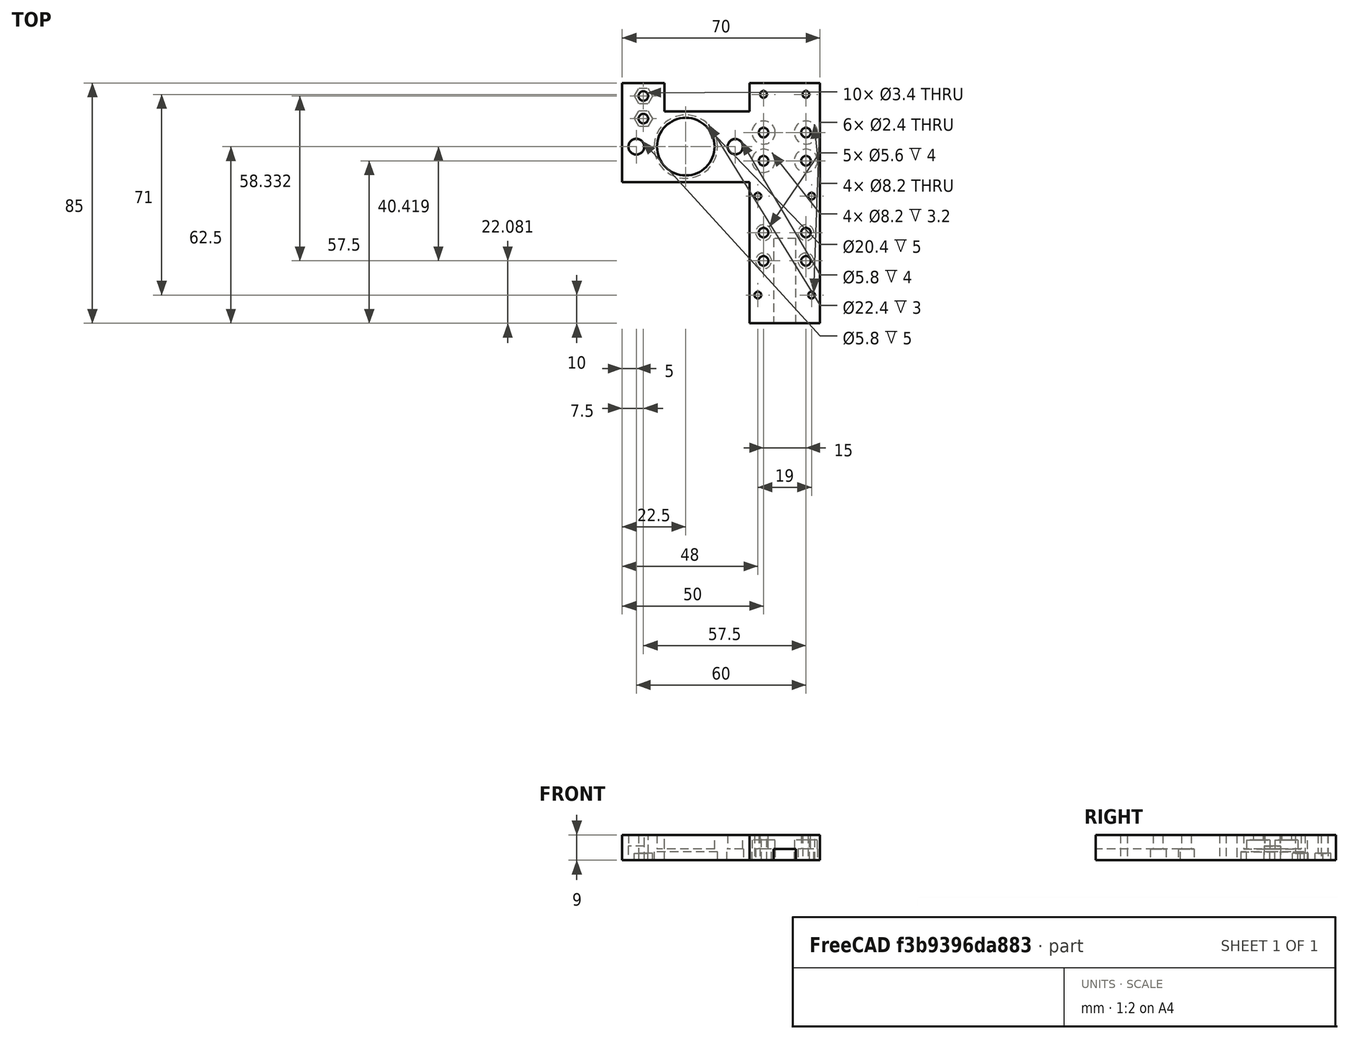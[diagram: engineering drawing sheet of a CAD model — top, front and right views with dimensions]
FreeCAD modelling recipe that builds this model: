
FCSTD DOCUMENT  (FreeCAD 0.18.4R)
Label: down_left_magnet_arm
License: All rights reserved
LicenseURL: http://en.wikipedia.org/wiki/All_rights_reserved
objects: Sketcher::SketchObject×15, PartDesign::Pocket×9, PartDesign::Pad×6, Mesh::Feature×1, PartDesign::Body×1
note: 46 computed .brp shape members not serialized (recipe doc carries the construction recipe); baked Part::Feature solids carry a one-line shape summary decoded from their .brp

FEATURE [Sketcher::SketchObject] Sketch
  MapMode = 5
  Support = -> [XY_Plane]
  sketch-geometry (10):
    g0: LineSegment StartX=-30 StartY=12.5 StartZ=0 EndX=30 EndY=12.5 EndZ=0
    g1: LineSegment StartX=30 StartY=12.5 StartZ=0 EndX=30 EndY=-12.5 EndZ=0
    g2: LineSegment StartX=30 StartY=-12.5 StartZ=0 EndX=-30 EndY=-12.5 EndZ=0
    g3: LineSegment StartX=-30 StartY=-12.5 StartZ=0 EndX=-30 EndY=12.5 EndZ=0
    g4: Circle CenterX=10 CenterY=5 CenterZ=0 NormalX=0 NormalY=0 NormalZ=1 AngleXU=0 Radius=1.7
    g5: Circle CenterX=25 CenterY=5 CenterZ=0 NormalX=0 NormalY=0 NormalZ=1 AngleXU=0 Radius=1.7
    g6: Circle CenterX=10 CenterY=-5 CenterZ=0 NormalX=0 NormalY=0 NormalZ=1 AngleXU=0 Radius=1.7
    g7: Circle CenterX=25 CenterY=-5 CenterZ=0 NormalX=0 NormalY=0 NormalZ=1 AngleXU=0 Radius=1.7
    g8: Circle CenterX=-17.5 CenterY=0 CenterZ=0 NormalX=0 NormalY=0 NormalZ=1 AngleXU=0 Radius=10.2
    g9: Circle CenterX=-9e-16 CenterY=0 CenterZ=0 NormalX=0 NormalY=0 NormalZ=1 AngleXU=0 Radius=2.7
  constraints (26):
    c: Coincident(g0,g1)
    c: Coincident(g1,g2)
    c: Coincident(g2,g3)
    c: Coincident(g3,g0)
    c: Horizontal(g2)
    c: Vertical(g1)
    c: Symmetric(g0,g0,g-2)
    c: Symmetric(g0,g2,g-1)
    c: DistanceX(g0,g0) = 60
    c: DistanceY(g3,g3) = 25
    c: Symmetric(g7,g5,g-1)
    c: Symmetric(g4,g6,g-1)
    c: Distance(g6,g7) = 15
    c: Distance(g4,g6) = 10
    c: Horizontal(g5,g4)
    c: Radius(g4) = 1.7
    c: Radius(g5) = 1.7
    c: Radius(g7) = 1.7
    c: Radius(g6) = 1.7
    c: Distance(g5,g1) = 5
    c: Radius(g8) = 10.2
    c: PointOnObject(g8,g-1)
    c: Distance(g8,g3) = 12.5
    c: PointOnObject(g9,g-1)
    c: Distance(g9,g8) = 17.5
    c: Radius(g9) = 2.7
FEATURE [PartDesign::Pad] Pad
  Length = 5
  Length2 = 100
  Profile = -> Sketch
  Type = 0
FEATURE [Sketcher::SketchObject] Sketch001
  ExternalGeometry = -> [Pad]
  MapMode = 5
  Placement = pos=(0,0,0) rot=(1,0,0;3.14159rad)
  Support = -> [Pad]
  sketch-geometry (4):
    g0: Circle CenterX=25 CenterY=5 CenterZ=0 NormalX=0 NormalY=0 NormalZ=1 AngleXU=0 Radius=4.1
    g1: Circle CenterX=25 CenterY=-5 CenterZ=0 NormalX=0 NormalY=0 NormalZ=1 AngleXU=0 Radius=4.1
    g2: Circle CenterX=10 CenterY=5 CenterZ=0 NormalX=0 NormalY=0 NormalZ=1 AngleXU=0 Radius=4.1
    g3: Circle CenterX=10 CenterY=-5 CenterZ=0 NormalX=0 NormalY=0 NormalZ=1 AngleXU=0 Radius=4.1
  constraints (8):
    c: Coincident(g0,g-4)
    c: Coincident(g1,g-5)
    c: Coincident(g2,g-6)
    c: Radius(g0) = 4.1
    c: Radius(g1) = 4.1
    c: Radius(g2) = 4.1
    c: Coincident(g3,g-11)
    c: Radius(g3) = 4.1
FEATURE [PartDesign::Pocket] Pocket001
  BaseFeature = -> Pad
  Length = 3.2
  Length2 = 100
  Profile = -> Sketch001
  Type = 0
FEATURE [Sketcher::SketchObject] Sketch002
  ExternalGeometry = -> [Pocket001]
  MapMode = 5
  Placement = pos=(0,0,0) rot=(1,0,0;3.14159rad)
  Support = -> [Pocket001]
  sketch-geometry (9):
    g0: LineSegment StartX=-30 StartY=12.5 StartZ=0 EndX=30 EndY=12.5 EndZ=0
    g1: LineSegment StartX=30 StartY=12.5 StartZ=0 EndX=30 EndY=-12.5 EndZ=0
    g2: LineSegment StartX=30 StartY=-12.5 StartZ=0 EndX=-30 EndY=-12.5 EndZ=0
    g3: LineSegment StartX=-30 StartY=-12.5 StartZ=0 EndX=-30 EndY=12.5 EndZ=0
    g4: Circle CenterX=0 CenterY=0 CenterZ=0 NormalX=0 NormalY=0 NormalZ=1 AngleXU=0 Radius=2.9
    g5: Circle CenterX=10 CenterY=5 CenterZ=0 NormalX=0 NormalY=0 NormalZ=1 AngleXU=0 Radius=4.1
    g6: Circle CenterX=10 CenterY=-5 CenterZ=0 NormalX=0 NormalY=0 NormalZ=1 AngleXU=0 Radius=4.1
    g7: Circle CenterX=25 CenterY=5 CenterZ=0 NormalX=0 NormalY=0 NormalZ=1 AngleXU=0 Radius=4.1
    g8: Circle CenterX=25 CenterY=-5 CenterZ=0 NormalX=0 NormalY=0 NormalZ=1 AngleXU=0 Radius=4.1
  constraints (20):
    c: Coincident(g0,g1)
    c: Coincident(g1,g2)
    c: Coincident(g2,g3)
    c: Coincident(g3,g0)
    c: Horizontal(g0)
    c: Horizontal(g2)
    c: Vertical(g1)
    c: Vertical(g3)
    c: Coincident(g0,g-6)
    c: Coincident(g1,g-5)
    c: Coincident(g4,g-1)
    c: Coincident(g5,g-8)
    c: Coincident(g6,g-9)
    c: Coincident(g7,g-10)
    c: Coincident(g8,g-11)
    c: Radius(g4) = 2.9
    c: Radius(g5) = 4.1
    c: Radius(g7) = 4.1
    c: Radius(g8) = 4.1
    c: Radius(g6) = 4.1
FEATURE [PartDesign::Pad] Pad001
  BaseFeature = -> Pocket001
  Length = 4
  Length2 = 100
  Profile = -> Sketch002
  Type = 0
FEATURE [Sketcher::SketchObject] Sketch003
  ExternalGeometry = -> [Pad001]
  MapMode = 5
  Placement = pos=(0,0,-4) rot=(1,0,0;3.14159rad)
  Support = -> [Pad001]
  sketch-geometry (1):
    g0: Circle CenterX=-17.5 CenterY=0 CenterZ=0 NormalX=0 NormalY=0 NormalZ=1 AngleXU=0 Radius=11.2
  constraints (3):
    c: PointOnObject(g0,g-1)
    c: Radius(g0) = 11.2
    c: Distance(g0,g-4) = 12.5
FEATURE [PartDesign::Pocket] Pocket
  BaseFeature = -> Pad001
  Length = 3
  Length2 = 100
  Profile = -> Sketch003
  Type = 0
FEATURE [Sketcher::SketchObject] Sketch004
  ExternalGeometry = -> [Pocket]
  MapMode = 5
  Placement = pos=(-30,0,0) rot=(0.57735,-0.57735,-0.57735;2.0944rad)
  Support = -> [Pocket]
  sketch-geometry (4):
    g0: LineSegment StartX=12.5 StartY=-4 StartZ=0 EndX=-12.5 EndY=-4 EndZ=0
    g1: LineSegment StartX=-12.5 StartY=-4 StartZ=0 EndX=-12.5 EndY=5 EndZ=0
    g2: LineSegment StartX=-12.5 StartY=5 StartZ=0 EndX=12.5 EndY=5 EndZ=0
    g3: LineSegment StartX=12.5 StartY=5 StartZ=0 EndX=12.5 EndY=-4 EndZ=0
  constraints (12):
    c: Coincident(g0,g1)
    c: Coincident(g1,g2)
    c: Coincident(g2,g3)
    c: Coincident(g3,g0)
    c: Horizontal(g2)
    c: Vertical(g1)
    c: Vertical(g3)
    c: PointOnObject(g0,g-3)
    c: DistanceX(g0,g0) = 25
    c: Symmetric(g0,g0,g-2)
    c: PointOnObject(g1,g-4)
    c: Distance(g-3) = 25
FEATURE [PartDesign::Pad] Pad002
  BaseFeature = -> Pocket
  Length = 10
  Length2 = 100
  Profile = -> Sketch004
  Type = 0
FEATURE [Sketcher::SketchObject] Sketch005
  ExternalGeometry = -> [Pad002]
  MapMode = 5
  Placement = pos=(0,0,-4) rot=(1,0,0;3.14159rad)
  Support = -> [Pad002]
  sketch-geometry (1):
    g0: Circle CenterX=-35 CenterY=0 CenterZ=0 NormalX=0 NormalY=0 NormalZ=1 AngleXU=0 Radius=2.9
  constraints (3):
    c: PointOnObject(g0,g-1)
    c: Distance(g-3,g0) = 17.5
    c: Radius(g0) = 2.9
FEATURE [PartDesign::Pocket] Pocket002
  BaseFeature = -> Pad002
  Length = 5
  Length2 = 100
  Profile = -> Sketch005
  Type = 0
FEATURE [Mesh::Feature] belt_support_left001
  Placement = pos=(-15,-17,5) rot=(0,0,1;0rad)
FEATURE [Sketcher::SketchObject] Sketch006
  ExternalGeometry = -> [Pocket002]
  MapMode = 5
  Placement = pos=(0,-12.5,0) rot=(1,0,0;1.5708rad)
  Support = -> [Pocket002]
  sketch-geometry (4):
    g0: LineSegment StartX=30 StartY=5 StartZ=0 EndX=5 EndY=5 EndZ=0
    g1: LineSegment StartX=5 StartY=5 StartZ=0 EndX=5 EndY=-4 EndZ=0
    g2: LineSegment StartX=5 StartY=-4 StartZ=0 EndX=30 EndY=-4 EndZ=0
    g3: LineSegment StartX=30 StartY=-4 StartZ=0 EndX=30 EndY=5 EndZ=0
  constraints (11):
    c: Coincident(g0,g1)
    c: Coincident(g1,g2)
    c: Coincident(g2,g3)
    c: Coincident(g3,g0)
    c: Horizontal(g0)
    c: Horizontal(g2)
    c: Vertical(g1)
    c: Vertical(g3)
    c: Coincident(g0,g-4)
    c: PointOnObject(g1,g-5)
    c: DistanceX(g0,g0) = 25
FEATURE [PartDesign::Pad] Pad003
  BaseFeature = -> Pocket002
  Length = 50
  Length2 = 100
  Profile = -> Sketch006
  Type = 0
FEATURE [Sketcher::SketchObject] Sketch007
  ExternalGeometry = -> [Pad003]
  MapMode = 5
  Placement = pos=(0,12.5,0) rot=(0,0.707107,0.707107;3.14159rad)
  Support = -> [Pad003]
  sketch-geometry (4):
    g0: LineSegment StartX=-30 StartY=5 StartZ=0 EndX=-5 EndY=5 EndZ=0
    g1: LineSegment StartX=-5 StartY=5 StartZ=0 EndX=-5 EndY=-4 EndZ=0
    g2: LineSegment StartX=-5 StartY=-4 StartZ=0 EndX=-30 EndY=-4 EndZ=0
    g3: LineSegment StartX=-30 StartY=-4 StartZ=0 EndX=-30 EndY=5 EndZ=0
  constraints (11):
    c: Coincident(g0,g1)
    c: Coincident(g1,g2)
    c: Coincident(g2,g3)
    c: Coincident(g3,g0)
    c: Horizontal(g0)
    c: Horizontal(g2)
    c: Vertical(g1)
    c: Vertical(g3)
    c: PointOnObject(g1,g-3)
    c: DistanceX(g0,g0) = 25
    c: Coincident(g-4,g0)
FEATURE [PartDesign::Pad] Pad004
  BaseFeature = -> Pad003
  Length = 10
  Length2 = 100
  Profile = -> Sketch007
  Type = 0
FEATURE [Sketcher::SketchObject] Sketch008
  ExternalGeometry = -> [Pad004]
  MapMode = 5
  Placement = pos=(0,-9e-16,-4) rot=(1,0,0;3.14159rad)
  Support = -> [Pad004]
  sketch-geometry (6):
    g0: Circle CenterX=10 CenterY=40.4193 CenterZ=0 NormalX=0 NormalY=0 NormalZ=1 AngleXU=0 Radius=1.7
    g1: Circle CenterX=25 CenterY=40.4193 CenterZ=0 NormalX=0 NormalY=0 NormalZ=1 AngleXU=0 Radius=1.7
    g2: Circle CenterX=10 CenterY=30.4193 CenterZ=0 NormalX=0 NormalY=0 NormalZ=1 AngleXU=0 Radius=1.7
    g3: Circle CenterX=25 CenterY=30.4193 CenterZ=0 NormalX=0 NormalY=0 NormalZ=1 AngleXU=0 Radius=1.7
    g4: Circle CenterX=10 CenterY=-18.5 CenterZ=0 NormalX=0 NormalY=0 NormalZ=1 AngleXU=0 Radius=1.2
    g5: Circle CenterX=25 CenterY=-18.5 CenterZ=0 NormalX=0 NormalY=0 NormalZ=1 AngleXU=0 Radius=1.2
  constraints (17):
    c: Horizontal(g0,g1)
    c: Horizontal(g2,g3)
    c: Horizontal(g4,g5)
    c: Vertical(g0,g2)
    c: Vertical(g2,g4)
    c: Vertical(g1,g3)
    c: Vertical(g3,g5)
    c: Radius(g0) = 1.7
    c: Radius(g1) = 1.7
    c: Radius(g2) = 1.7
    c: Radius(g3) = 1.7
    c: Radius(g4) = 1.2
    c: Radius(g5) = 1.2
    c: Distance(g0,g1) = 15
    c: Vertical(g2,g-3)
    c: Distance(g2,g0) = 10
    c: Distance(g4,g-4) = 6
FEATURE [PartDesign::Pocket] Pocket003
  BaseFeature = -> Pad004
  Length = 9
  Length2 = 100
  Profile = -> Sketch008
  Type = 0
FEATURE [Sketcher::SketchObject] Sketch009
  ExternalGeometry = -> [Pocket003]
  MapMode = 5
  Placement = pos=(0,-9e-16,-4) rot=(1,0,0;3.14159rad)
  Support = -> [Pocket003]
  sketch-geometry (8):
    g0: LineSegment StartX=13.5 StartY=72.5 StartZ=0 EndX=21.5 EndY=72.5 EndZ=0
    g1: LineSegment StartX=21.5 StartY=72.5 StartZ=0 EndX=21.5 EndY=32.5 EndZ=0
    g2: LineSegment StartX=21.5 StartY=32.5 StartZ=0 EndX=13.5 EndY=32.5 EndZ=0
    g3: LineSegment StartX=13.5 StartY=32.5 StartZ=0 EndX=13.5 EndY=72.5 EndZ=0
    g4: Circle CenterX=10 CenterY=40.4193 CenterZ=0 NormalX=0 NormalY=0 NormalZ=1 AngleXU=0 Radius=2.8
    g5: Circle CenterX=10 CenterY=30.4193 CenterZ=0 NormalX=0 NormalY=0 NormalZ=1 AngleXU=0 Radius=2.8
    g6: Circle CenterX=25 CenterY=40.4193 CenterZ=0 NormalX=0 NormalY=0 NormalZ=1 AngleXU=0 Radius=2.8
    g7: Circle CenterX=25 CenterY=30.4193 CenterZ=0 NormalX=0 NormalY=0 NormalZ=1 AngleXU=0 Radius=2.8
  constraints (20):
    c: Coincident(g0,g1)
    c: Coincident(g1,g2)
    c: Coincident(g2,g3)
    c: Coincident(g3,g0)
    c: Horizontal(g0)
    c: Horizontal(g2)
    c: Vertical(g1)
    c: Vertical(g3)
    c: DistanceX(g2,g2) = 8
    c: DistanceY(g3,g3) = 40
    c: Distance(g1,g-3) = 20
    c: Distance(g-4,g3) = 3.5
    c: Coincident(g4,g-7)
    c: Coincident(g5,g-4)
    c: Coincident(g6,g-6)
    c: Coincident(g7,g-5)
    c: Radius(g6) = 2.8
    c: Radius(g4) = 2.8
    c: Radius(g5) = 2.8
    c: Radius(g7) = 2.8
FEATURE [PartDesign::Pocket] Pocket004
  BaseFeature = -> Pocket003
  Length = 4
  Length2 = 100
  Profile = -> Sketch009
  Type = 0
FEATURE [Sketcher::SketchObject] Sketch010
  ExternalGeometry = -> [Pocket004]
  MapMode = 5
  Placement = pos=(0,-9e-16,-4) rot=(1,0,0;3.14159rad)
  Support = -> [Pocket004]
  sketch-geometry (4):
    g0: Circle CenterX=27 CenterY=52.5 CenterZ=0 NormalX=0 NormalY=0 NormalZ=1 AngleXU=0 Radius=1.2
    g1: Circle CenterX=8 CenterY=17.5 CenterZ=0 NormalX=0 NormalY=0 NormalZ=1 AngleXU=0 Radius=1.2
    g2: Circle CenterX=27 CenterY=17.5 CenterZ=0 NormalX=0 NormalY=0 NormalZ=1 AngleXU=0 Radius=1.2
    g3: Circle CenterX=8 CenterY=52.5 CenterZ=0 NormalX=0 NormalY=0 NormalZ=1 AngleXU=0 Radius=1.2
  constraints (12):
    c: Radius(g0) = 1.2
    c: Radius(g1) = 1.2
    c: Radius(g2) = 1.2
    c: Horizontal(g1,g2)
    c: Vertical(g0,g2)
    c: Distance(g1,g2) = 19
    c: Horizontal(g3,g0)
    c: Radius(g3) = 1.2
    c: Distance(g3,g0) = 19
    c: Distance(g3,g-6) = 3
    c: Distance(g3,g-4) = 10
    c: Distance(g1,g-3) = 5
FEATURE [PartDesign::Pocket] Pocket005
  BaseFeature = -> Pocket004
  Length = 9
  Length2 = 100
  Profile = -> Sketch010
  Type = 0
FEATURE [Sketcher::SketchObject] Sketch011
  ExternalGeometry = -> [Pocket005]
  MapMode = 5
  Placement = pos=(0,0,1) rot=(1,0,0;3.14159rad)
  Support = -> [Pocket005]
  sketch-geometry (1):
    g0: Circle CenterX=-35 CenterY=0 CenterZ=0 NormalX=0 NormalY=0 NormalZ=1 AngleXU=0 Radius=2.8
  constraints (2):
    c: Coincident(g0,g-3)
    c: Radius(g0) = 2.8
FEATURE [PartDesign::Pocket] Pocket006
  BaseFeature = -> Pocket005
  Length = 4
  Length2 = 100
  Profile = -> Sketch011
  Type = 0
FEATURE [Sketcher::SketchObject] Sketch013
  ExternalGeometry = -> [Pocket006]
  MapMode = 5
  Placement = pos=(0,12.5,0) rot=(0,0.707107,0.707107;3.14159rad)
  Support = -> [Pocket006]
  sketch-geometry (4):
    g0: LineSegment StartX=40 StartY=-4 StartZ=0 EndX=25 EndY=-4 EndZ=0
    g1: LineSegment StartX=25 StartY=-4 StartZ=0 EndX=25 EndY=5 EndZ=0
    g2: LineSegment StartX=25 StartY=5 StartZ=0 EndX=40 EndY=5 EndZ=0
    g3: LineSegment StartX=40 StartY=5 StartZ=0 EndX=40 EndY=-4 EndZ=0
  constraints (11):
    c: Coincident(g0,g1)
    c: Coincident(g1,g2)
    c: Coincident(g2,g3)
    c: Coincident(g3,g0)
    c: Horizontal(g0)
    c: Horizontal(g2)
    c: Vertical(g1)
    c: Vertical(g3)
    c: Coincident(g0,g-4)
    c: PointOnObject(g1,g-5)
    c: DistanceX(g2,g2) = 15
FEATURE [PartDesign::Pad] Pad005
  BaseFeature = -> Pocket006
  Length = 10
  Length2 = 100
  Profile = -> Sketch013
  Type = 0
FEATURE [Sketcher::SketchObject] Sketch014
  ExternalGeometry = -> [Pad005]
  MapMode = 5
  Placement = pos=(0,-9e-16,-4) rot=(1,0,0;3.14159rad)
  Support = -> [Pad005]
  sketch-geometry (14):
    g0: LineSegment StartX=-30.9 StartY=-12.6838 StartZ=0 EndX=-29.3 EndY=-9.91247 EndZ=0
    g1: LineSegment StartX=-29.3 StartY=-9.91247 StartZ=0 EndX=-30.9 EndY=-7.14119 EndZ=0
    g2: LineSegment StartX=-30.9 StartY=-7.14119 StartZ=0 EndX=-34.1 EndY=-7.14119 EndZ=0
    g3: LineSegment StartX=-34.1 StartY=-7.14119 StartZ=0 EndX=-35.7 EndY=-9.91247 EndZ=0
    g4: LineSegment StartX=-35.7 StartY=-9.91247 StartZ=0 EndX=-34.1 EndY=-12.6838 EndZ=0
    g5: LineSegment StartX=-34.1 StartY=-12.6838 StartZ=0 EndX=-30.9 EndY=-12.6838 EndZ=0
    g6: Circle [constr] CenterX=-32.5 CenterY=-9.91247 CenterZ=0 NormalX=0 NormalY=0 NormalZ=1 AngleXU=0 Radius=3.2
    g7: LineSegment StartX=-30.9 StartY=-20.6838 StartZ=0 EndX=-29.3 EndY=-17.9125 EndZ=0
    g8: LineSegment StartX=-29.3 StartY=-17.9125 StartZ=0 EndX=-30.9 EndY=-15.1412 EndZ=0
    g9: LineSegment StartX=-30.9 StartY=-15.1412 StartZ=0 EndX=-34.1 EndY=-15.1412 EndZ=0
    g10: LineSegment StartX=-34.1 StartY=-15.1412 StartZ=0 EndX=-35.7 EndY=-17.9125 EndZ=0
    g11: LineSegment StartX=-35.7 StartY=-17.9125 StartZ=0 EndX=-34.1 EndY=-20.6838 EndZ=0
    g12: LineSegment StartX=-34.1 StartY=-20.6838 StartZ=0 EndX=-30.9 EndY=-20.6838 EndZ=0
    g13: Circle [constr] CenterX=-32.5 CenterY=-17.9125 CenterZ=0 NormalX=0 NormalY=0 NormalZ=1 AngleXU=0 Radius=3.2
  constraints (33):
    c: Coincident(g0,g1)
    c: Coincident(g1,g2)
    c: Coincident(g2,g3)
    c: Coincident(g3,g4)
    c: Coincident(g4,g5)
    c: Coincident(g5,g0)
    c: Equal(g0, g1-g5) x5
    c: PointOnObject(g0,g6)
    c: PointOnObject(g1,g6)
    c: PointOnObject(g2,g6)
    c: PointOnObject(g3,g6)
    c: PointOnObject(g4,g6)
    c: PointOnObject(g5,g6)
    c: Coincident(g7,g8)
    c: Coincident(g8,g9)
    c: Coincident(g9,g10)
    c: Coincident(g10,g11)
    c: Coincident(g11,g12)
    c: Coincident(g12,g7)
    c: Equal(g7, g8-g12) x5
    c: PointOnObject(g7,g13)
    c: PointOnObject(g8,g13)
    c: PointOnObject(g9,g13)
    c: PointOnObject(g10,g13)
    c: PointOnObject(g11,g13)
    c: PointOnObject(g12,g13)
    c: Vertical(g13,g6)
    c: Radius(g6) = 3.2
    c: Radius(g13) = 3.2
    c: Distance(g13,g6) = 8
    c: Vertical(g0,g8)
    c: Distance(g13,g-4) = 7.5
    c: Parallel(g9,g5)
FEATURE [PartDesign::Pocket] Pocket007
  BaseFeature = -> Pad005
  Length = 2.5
  Length2 = 100
  Profile = -> Sketch014
  Type = 0
FEATURE [Sketcher::SketchObject] Sketch015
  ExternalGeometry = -> [Pocket007]
  MapMode = 5
  Placement = pos=(0,-2e-16,-1.5) rot=(1,0,0;3.14159rad)
  Support = -> [Pocket007]
  sketch-geometry (2):
    g0: Circle CenterX=-32.5 CenterY=-9.91247 CenterZ=0 NormalX=0 NormalY=0 NormalZ=1 AngleXU=0 Radius=1.7
    g1: Circle CenterX=-32.5 CenterY=-17.9125 CenterZ=0 NormalX=0 NormalY=0 NormalZ=1 AngleXU=0 Radius=1.7
  constraints (7):
    c: Radius(g1) = 1.7
    c: Radius(g0) = 1.7
    c: Distance(g-4,g-3) = 6.4
    c: Distance(g0,g-3) = 3.2
    c: Distance(g0,g-3) = 3.2
    c: Distance(g1,g-5) = 3.2
    c: Distance(g1,g-6) = 3.2
FEATURE [PartDesign::Pocket] Pocket008
  BaseFeature = -> Pocket007
  Length = 7
  Length2 = 100
  Profile = -> Sketch015
  Type = 0
FEATURE [PartDesign::Body] Body
  Group = -> [Sketch,Pad,Sketch001,Pocket001,Sketch002,Pad001,Sketch003,Pocket,Sketch004,Pad002,Sketch005,Pocket002,Sketch006,Pad003,Sketch007,Pad004,Sketch008,Pocket003,Sketch009,Pocket004,Sketch010,Pocket005,Sketch011,Pocket006,Sketch013,Pad005,Sketch014,Pocket007,Sketch015,Pocket008]
  Origin = -> Origin
  Tip = -> Pocket008
